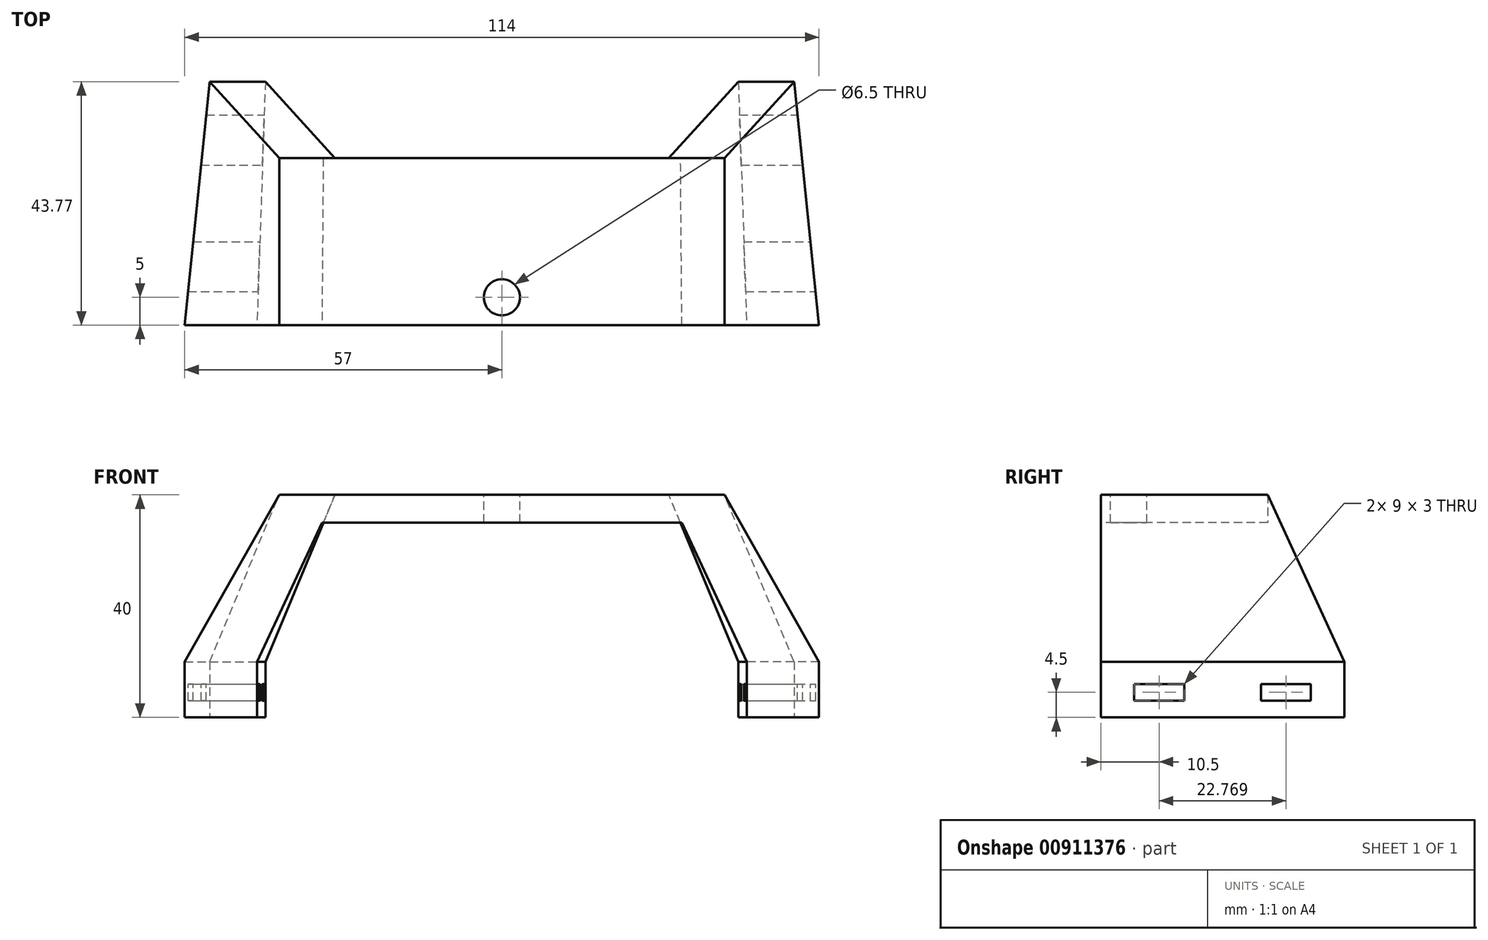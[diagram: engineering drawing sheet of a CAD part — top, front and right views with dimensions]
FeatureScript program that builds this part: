
annotation { "Feature Type Name" : "Feature", "Feature Type Description" : "" }
export const myFeature = defineFeature(function(context is Context, id is Id, definition is map)
    precondition{}
    {
        {
            var Q0;
            Q0=qCreatedBy(makeId("Top.planeOp"),FACE);
            var sketch = newSketch(context, id + "F0", { "sketchPlane" : qUnion([Q0])});
            skLineSegment(sketch, "E0", {"start": v(-57, 0) * mm, "end": v(-52.5, 43.77) * mm});
            skLineSegment(sketch, "E1", {"start": v(-52.5, 43.77) * mm, "end": v(-42.5, 43.77) * mm});
            skLineSegment(sketch, "E2", {"start": v(-42.5, 43.77) * mm, "end": v(-44, 0) * mm});
            skLineSegment(sketch, "E3", {"start": v(-44, 0) * mm, "end": v(-57, 0) * mm});
            skLineSegment(sketch, "E4.MirrorCS", {"start": v(44, 0) * mm, "end": v(57, 0) * mm});
            skLineSegment(sketch, "E5.MirrorCS", {"start": v(42.5, 43.77) * mm, "end": v(44, 0) * mm});
            skLineSegment(sketch, "E6.MirrorCS", {"start": v(57, 0) * mm, "end": v(52.5, 43.77) * mm});
            skLineSegment(sketch, "E7.MirrorCS", {"start": v(52.5, 43.77) * mm, "end": v(42.5, 43.77) * mm});
            skSolve(sketch);
        }
        {
            var Q0;
            Q0=makeQuery(id+"F0.imprint","IMPRINT",FACE,{"disambiguationData":[TD([[makeQuery(id+"F0.imprint","IMPRINT",EDGE,{"derivedFrom":sQuery(id+"F0.wireOp",EDGE,"E0")}),-1.0]])]});
            var Q1;
            Q1=makeQuery(id+"F0.imprint","IMPRINT",FACE,{"disambiguationData":[TD([[makeQuery(id+"F0.imprint","IMPRINT",EDGE,{"derivedFrom":sQuery(id+"F0.wireOp",EDGE,"E4.MirrorCS")}),1.0]])]});
            extrude(context, id + "F1", {"entities" : qUnion([Q0, Q1]), "depth" : 10 * mm, "offsetDistance" : 25 * mm});
        }
        {
            var Q0;
            Q0=qCreatedBy(makeId("Top.planeOp"),FACE);
            cPlane(context, id + "F2", {"entities" : qUnion([Q0]), "cplaneType" : CPlaneType.OFFSET, "offset" : 40 * mm, "width" : 150 * mm, "height" : 150 * mm});
        }
        {
            var Q0;
            Q0=qCreatedBy(id+"F2.planeOp",FACE);
            var sketch = newSketch(context, id + "F3", { "sketchPlane" : qUnion([Q0])});
            skLineSegment(sketch, "E8.bottom", {"start": v(-40, 0) * mm, "end": v(-30, 0) * mm});
            skLineSegment(sketch, "E8.top", {"start": v(-40, 30) * mm, "end": v(-30, 30) * mm});
            skLineSegment(sketch, "E8.left", {"start": v(-40, 0) * mm, "end": v(-40, 30) * mm});
            skLineSegment(sketch, "E8.right", {"start": v(-30, 0) * mm, "end": v(-30, 30) * mm});
            skLineSegment(sketch, "E9.MirrorCS", {"start": v(40, 0) * mm, "end": v(30, 0) * mm});
            skLineSegment(sketch, "E10.MirrorCS", {"start": v(30, 0) * mm, "end": v(30, 30) * mm});
            skLineSegment(sketch, "E11.MirrorCS", {"start": v(40, 0) * mm, "end": v(40, 30) * mm});
            skLineSegment(sketch, "E12.MirrorCS", {"start": v(40, 30) * mm, "end": v(30, 30) * mm});
            skSolve(sketch);
        }
        {
            var Q1;
            Q1=makeQuery(id+"F1.opExtrude","CAP_FACE",FACE,{"disambiguationData":[OSD([sQuery(id+"F0.wireOp",EDGE,"E0"),sQuery(id+"F0.wireOp",EDGE,"E1"),sQuery(id+"F0.wireOp",EDGE,"E2"),sQuery(id+"F0.wireOp",EDGE,"E3")])],"isStart":false});
            var Q2;
            Q2=makeQuery(id+"F3.imprint","IMPRINT",FACE,{"disambiguationData":[TD([[makeQuery(id+"F3.imprint","IMPRINT",EDGE,{"derivedFrom":sQuery(id+"F3.wireOp",EDGE,"E8.bottom")}),1.0]])]});
            loft(context, id + "F4", {"operationType" : NewBodyOperationType.ADD, "sheetProfilesArray" : [{ "sheetProfileEntities" : qUnion([Q1]) }, { "sheetProfileEntities" : qUnion([Q2]) }]});
        }
        {
            var Q1;
            Q1=makeQuery(id+"F1.opExtrude","CAP_FACE",FACE,{"disambiguationData":[OSD([sQuery(id+"F0.wireOp",EDGE,"E4.MirrorCS"),sQuery(id+"F0.wireOp",EDGE,"E5.MirrorCS"),sQuery(id+"F0.wireOp",EDGE,"E6.MirrorCS"),sQuery(id+"F0.wireOp",EDGE,"E7.MirrorCS")])],"isStart":false});
            var Q2;
            Q2=makeQuery(id+"F3.imprint","IMPRINT",FACE,{"disambiguationData":[TD([[makeQuery(id+"F3.imprint","IMPRINT",EDGE,{"derivedFrom":sQuery(id+"F3.wireOp",EDGE,"E9.MirrorCS")}),-1.0]])]});
            loft(context, id + "F5", {"operationType" : NewBodyOperationType.ADD, "sheetProfilesArray" : [{ "sheetProfileEntities" : qUnion([Q1]) }, { "sheetProfileEntities" : qUnion([Q2]) }]});
        }
        {
            var Q0;
            Q0=qCreatedBy(id+"F2.planeOp",FACE);
            var sketch = newSketch(context, id + "F6", { "sketchPlane" : qUnion([Q0])});
            skPoint(sketch, "E13.0", {"position": v(-40, 30) * mm});
            skPoint(sketch, "E14.0", {"position": v(40, 0) * mm});
            skLineSegment(sketch, "E15.bottom", {"start": v(-40, 30) * mm, "end": v(40, 30) * mm});
            skLineSegment(sketch, "E15.top", {"start": v(-40, 0) * mm, "end": v(40, 0) * mm});
            skLineSegment(sketch, "E15.left", {"start": v(-40, 30) * mm, "end": v(-40, 0) * mm});
            skLineSegment(sketch, "E15.right", {"start": v(40, 30) * mm, "end": v(40, 0) * mm});
            skSolve(sketch);
        }
        {
            var Q0;
            Q0 = qSketchRegion(id + "F6", true);
            extrude(context, id + "F7", {"entities" : qUnion([Q0]), "operationType" : NewBodyOperationType.ADD, "oppositeDirection" : true, "depth" : 5 * mm, "offsetDistance" : 25 * mm});
        }
        {
            var Q0;
            Q0=qCreatedBy(id+"F2.planeOp",FACE);
            var sketch = newSketch(context, id + "F8", { "sketchPlane" : qUnion([Q0])});
            skCircle(sketch, "E16", {"center": v(0, 5) * mm, "radius": 3.25 * mm});
            skSolve(sketch);
        }
        {
            var Q0;
            Q0 = qSketchRegion(id + "F8", true);
            var Q1;
            Q1=makeQuery(id+"F7.opExtrude","CAP_FACE",FACE,{"disambiguationData":[OSD([sQuery(id+"F6.wireOp",EDGE,"E15.bottom"),sQuery(id+"F6.wireOp",EDGE,"E15.top"),sQuery(id+"F6.wireOp",EDGE,"E15.left"),sQuery(id+"F6.wireOp",EDGE,"E15.right")])],"isStart":false});
            extrude(context, id + "F9", {"entities" : qUnion([Q0]), "operationType" : NewBodyOperationType.REMOVE, "endBound" : BoundingType.UP_TO_SURFACE, "oppositeDirection" : true, "depth" : 25 * mm, "endBoundEntityFace" : qUnion([Q1]), "offsetDistance" : 25 * mm});
        }
        {
            var Q0;
            Q0=qCreatedBy(makeId("Right.planeOp"),FACE);
            var sketch = newSketch(context, id + "F10", { "sketchPlane" : qUnion([Q0])});
            skLineSegment(sketch, "E17.bottom", {"start": v(6, 6) * mm, "end": v(15, 6) * mm});
            skLineSegment(sketch, "E17.top", {"start": v(6, 3) * mm, "end": v(15, 3) * mm});
            skLineSegment(sketch, "E17.left", {"start": v(6, 6) * mm, "end": v(6, 3) * mm});
            skLineSegment(sketch, "E17.right", {"start": v(15, 6) * mm, "end": v(15, 3) * mm});
            skLineSegment(sketch, "E18.bottom", {"start": v(28.77, 6) * mm, "end": v(37.77, 6) * mm});
            skLineSegment(sketch, "E18.top", {"start": v(28.77, 3) * mm, "end": v(37.77, 3) * mm});
            skLineSegment(sketch, "E18.left", {"start": v(28.77, 6) * mm, "end": v(28.77, 3) * mm});
            skLineSegment(sketch, "E18.right", {"start": v(37.77, 6) * mm, "end": v(37.77, 3) * mm});
            skSolve(sketch);
        }
        {
            var Q0;
            Q0=makeQuery(id+"F10.imprint","IMPRINT",FACE,{"disambiguationData":[TD([[makeQuery(id+"F10.imprint","IMPRINT",EDGE,{"derivedFrom":sQuery(id+"F10.wireOp",EDGE,"E17.bottom")}),-1.0]])]});
            var Q1;
            Q1=makeQuery(id+"F10.imprint","IMPRINT",FACE,{"disambiguationData":[TD([[makeQuery(id+"F10.imprint","IMPRINT",EDGE,{"derivedFrom":sQuery(id+"F10.wireOp",EDGE,"E18.bottom")}),-1.0]])]});
            extrude(context, id + "F11", {"entities" : qUnion([Q0, Q1]), "operationType" : NewBodyOperationType.REMOVE, "endBound" : BoundingType.SYMMETRIC, "oppositeDirection" : true, "depth" : 200 * mm, "offsetDistance" : 25 * mm});
        }
    });
